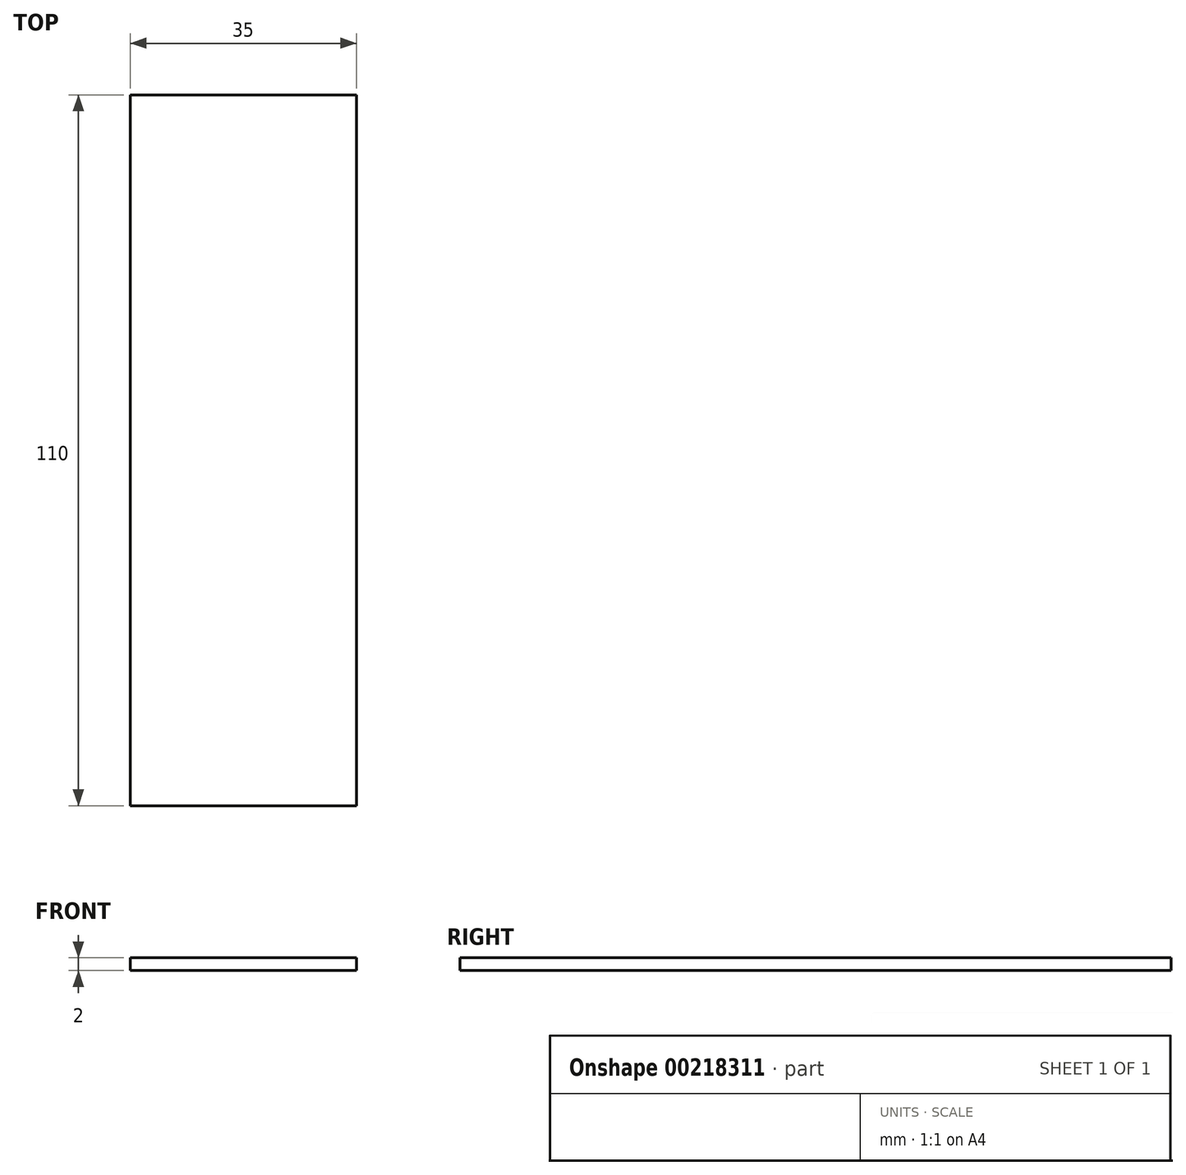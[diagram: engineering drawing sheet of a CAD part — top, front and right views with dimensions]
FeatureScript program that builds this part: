
annotation { "Feature Type Name" : "Feature", "Feature Type Description" : "" }
export const myFeature = defineFeature(function(context is Context, id is Id, definition is map)
    precondition{}
    {
        {
            var Q0;
            Q0=qCreatedBy(makeId("Top.planeOp"),FACE);
            var sketch = newSketch(context, id + "F0", { "sketchPlane" : qUnion([Q0])});
            skLineSegment(sketch, "E0.bottom", {"start": v(17.5, -55) * mm, "end": v(-17.5, -55) * mm});
            skLineSegment(sketch, "E0.top", {"start": v(17.5, 55) * mm, "end": v(-17.5, 55) * mm});
            skLineSegment(sketch, "E0.left", {"start": v(17.5, -55) * mm, "end": v(17.5, 55) * mm});
            skLineSegment(sketch, "E0.right", {"start": v(-17.5, -55) * mm, "end": v(-17.5, 55) * mm});
            skPoint(sketch, "E0.middle", {"position": v(0, 0) * mm});
            skSolve(sketch);
        }
        {
            var Q0;
            Q0 = qSketchRegion(id + "F0", true);
            extrude(context, id + "F1", {"entities" : qUnion([Q0]), "depth" : 2 * mm, "offsetDistance" : 25 * mm});
        }
    });
